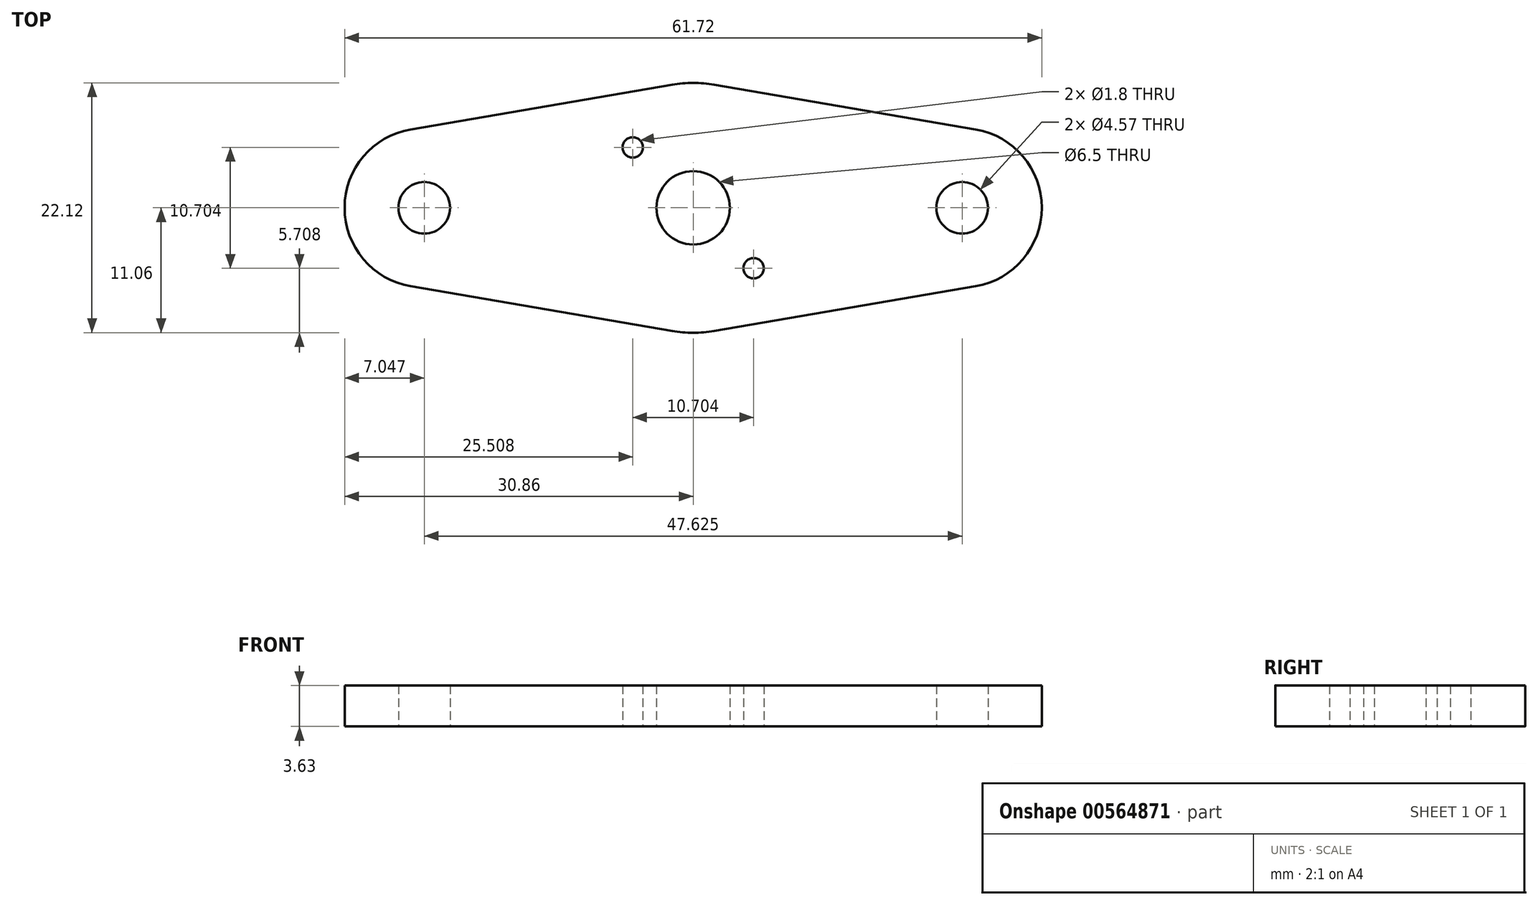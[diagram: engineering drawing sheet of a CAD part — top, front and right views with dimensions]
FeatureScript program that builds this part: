
annotation { "Feature Type Name" : "Feature", "Feature Type Description" : "" }
export const myFeature = defineFeature(function(context is Context, id is Id, definition is map)
    precondition{}
    {
        {
            var Q0;
            Q0=qCreatedBy(makeId("Top.planeOp"),FACE);
            var sketch = newSketch(context, id + "F0", { "sketchPlane" : qUnion([Q0])});
            skCircle(sketch, "E0", {"center": v(0, 0) * mm, "radius": 3.25 * mm});
            skArc(sketch, "E1", {"start": v(1.86, 10.9) * mm, "mid": v(0, 11.06) * mm, "end": v(-1.86, 10.9) * mm});
            skCircle(sketch, "E2", {"center": v(0, 0) * mm, "radius": 23.81 * mm, "construction": true});
            skCircle(sketch, "E3", {"center": v(23.81, 0) * mm, "radius": 2.29 * mm});
            skLineSegment(sketch, "E4", {"start": v(0, 0) * mm, "end": v(0, 19.6) * mm, "construction": true});
            skArc(sketch, "E5.0", {"start": v(25, -6.95) * mm, "mid": v(30.86, 0) * mm, "end": v(25, 6.95) * mm});
            skCircle(sketch, "E6", {"center": v(-5.35, 5.35) * mm, "radius": 0.9 * mm});
            skLineSegment(sketch, "E7", {"start": v(1.86, 10.9) * mm, "end": v(25, 6.95) * mm});
            skLineSegment(sketch, "E8", {"start": v(0, 0) * mm, "end": v(23.81, 0) * mm, "construction": true});
            skLineSegment(sketch, "E9.MirrorCS", {"start": v(1.86, -10.9) * mm, "end": v(25, -6.95) * mm});
            skCircle(sketch, "E10", {"center": v(0, 0) * mm, "radius": 7.57 * mm, "construction": true});
            skLineSegment(sketch, "E11", {"start": v(-5.35, 5.35) * mm, "end": v(0, 0) * mm});
            skCircle(sketch, "E12.1.0", {"center": v(5.35, -5.35) * mm, "radius": 0.9 * mm});
            skLineSegment(sketch, "E13.MirrorCS", {"start": v(-1.86, 10.9) * mm, "end": v(-25, 6.95) * mm});
            skArc(sketch, "E14.MirrorCS", {"start": v(-25, -6.95) * mm, "mid": v(-30.86, 0) * mm, "end": v(-25, 6.95) * mm});
            skLineSegment(sketch, "E15.MirrorCS", {"start": v(-1.86, -10.9) * mm, "end": v(-25, -6.95) * mm});
            skArc(sketch, "E16.trimOffspring", {"start": v(-1.86, -10.9) * mm, "mid": v(0, -11.06) * mm, "end": v(1.86, -10.9) * mm});
            skCircle(sketch, "E17.1.0", {"center": v(-23.81, 0) * mm, "radius": 2.29 * mm});
            skSolve(sketch);
        }
        {
            var Q0;
            Q0=makeQuery(id+"F0.imprint","IMPRINT",FACE,{"disambiguationData":[TD([[makeQuery(id+"F0.imprint","IMPRINT",EDGE,{"derivedFrom":sQuery(id+"F0.wireOp",EDGE,"E0")}),-1.0]])]});
            extrude(context, id + "F1", {"entities" : qUnion([Q0]), "depth" : 3.63 * mm, "offsetDistance" : 25.4 * mm});
        }
    });
